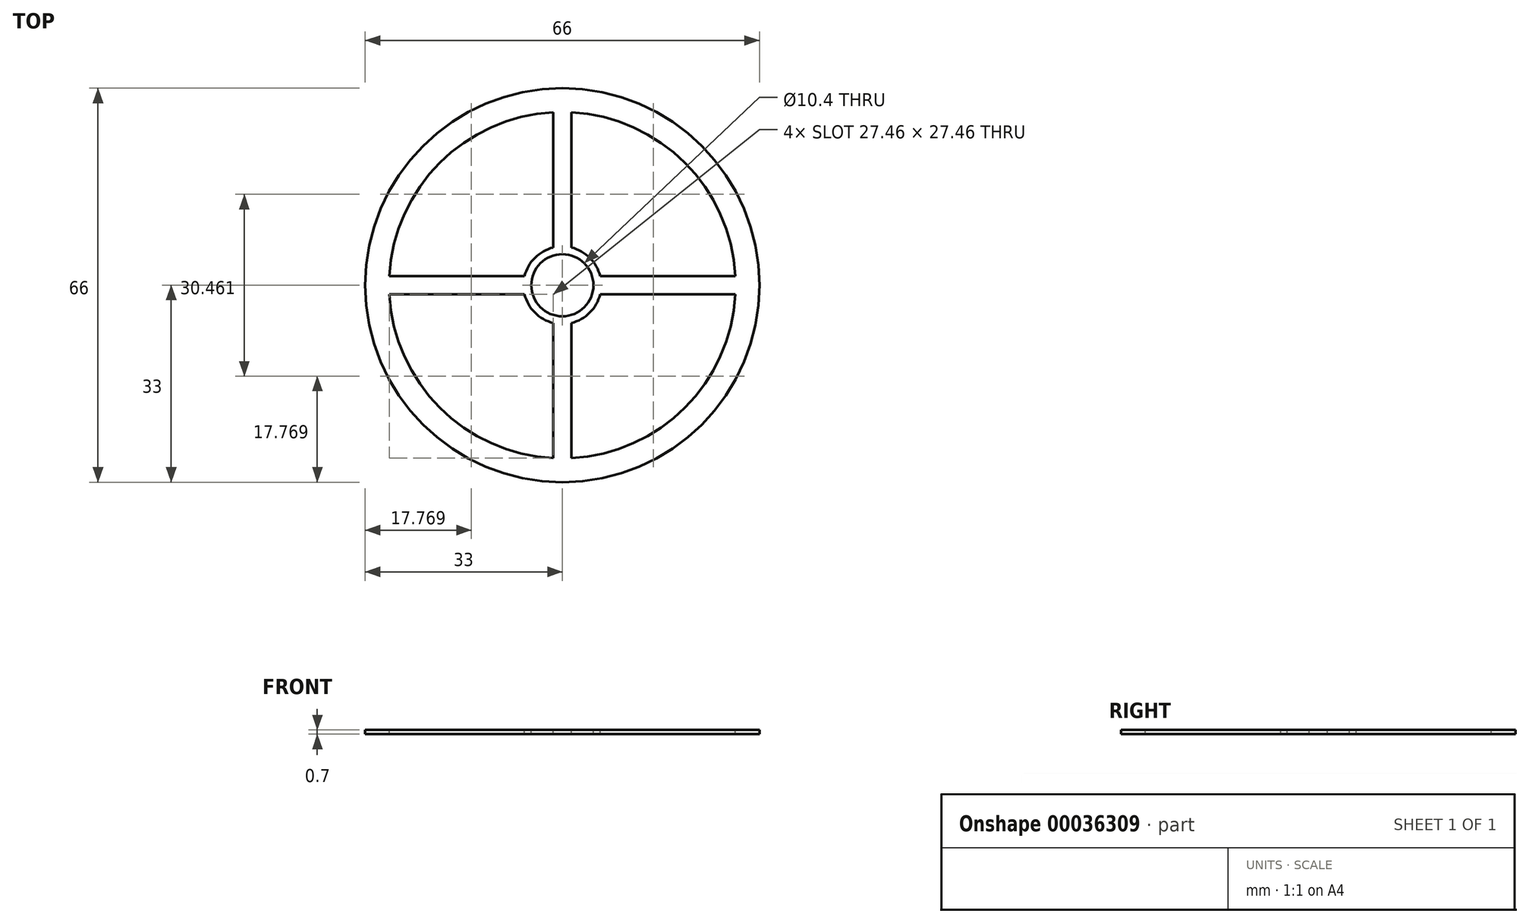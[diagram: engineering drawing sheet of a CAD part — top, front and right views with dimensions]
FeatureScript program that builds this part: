
annotation { "Feature Type Name" : "Feature", "Feature Type Description" : "" }
export const myFeature = defineFeature(function(context is Context, id is Id, definition is map)
    precondition{}
    {
        {
            var Q0;
            Q0=qCreatedBy(makeId("Top.planeOp"),FACE);
            var sketch = newSketch(context, id + "F0", { "sketchPlane" : qUnion([Q0])});
            skCircle(sketch, "E0", {"center": v(0, 0) * mm, "radius": 33 * mm});
            skSolve(sketch);
        }
        {
            var Q0;
            Q0=qSketchRegion(id+"F0",true);
            extrude(context, id + "F1", {"entities" : qUnion([Q0]), "depth" : 0.7 * mm});
        }
        {
            var Q0;
            Q0=makeQuery(id+"F1.opExtrude","CAP_FACE",FACE,{"disambiguationData":[OSD([sQuery(id+"F0.wireOp",EDGE,"E0")])],"isStart":false});
            var sketch = newSketch(context, id + "F2", { "sketchPlane" : qUnion([Q0])});
            skCircle(sketch, "E1", {"center": v(0, 0) * mm, "radius": 5.2 * mm});
            skSolve(sketch);
        }
        {
            var Q0;
            Q0=makeQuery(id+"F2.imprint","IMPRINT",FACE,{"disambiguationData":[TD([[makeQuery(id+"F2.imprint","IMPRINT",EDGE,{"derivedFrom":sQuery(id+"F2.wireOp",EDGE,"E1")}),1.0]])]});
            extrude(context, id + "F3", {"entities" : qUnion([Q0]), "operationType" : NewBodyOperationType.REMOVE, "endBound" : BoundingType.UP_TO_NEXT, "oppositeDirection" : true, "depth" : 25 * mm});
        }
        {
            var Q0;
            Q0=makeQuery(id+"F1.opExtrude","CAP_FACE",FACE,{"disambiguationData":[OSD([sQuery(id+"F0.wireOp",EDGE,"E0")])],"isStart":false});
            var sketch = newSketch(context, id + "F4", { "sketchPlane" : qUnion([Q0])});
            skCircle(sketch, "E2", {"center": v(0, 0) * mm, "radius": 29 * mm});
            skCircle(sketch, "E3", {"center": v(0, 0) * mm, "radius": 6.5 * mm});
            skLineSegment(sketch, "E4", {"start": v(0, -6.5) * mm, "end": v(0, -29) * mm, "construction": true});
            skLineSegment(sketch, "E5", {"start": v(-6.5, 0) * mm, "end": v(-29, 0) * mm, "construction": true});
            skLineSegment(sketch, "E6", {"start": v(0, 6.5) * mm, "end": v(0, 29) * mm, "construction": true});
            skLineSegment(sketch, "E7", {"start": v(6.5, 0) * mm, "end": v(29, 0) * mm, "construction": true});
            skLineSegment(sketch, "E8.0", {"start": v(1.5, 6.32) * mm, "end": v(1.5, 28.96) * mm});
            skLineSegment(sketch, "E9.0", {"start": v(-1.5, 6.32) * mm, "end": v(-1.5, 28.96) * mm});
            skLineSegment(sketch, "E10", {"start": v(1.5, -6.32) * mm, "end": v(1.5, -28.96) * mm});
            skLineSegment(sketch, "E11", {"start": v(-1.5, -6.32) * mm, "end": v(-1.5, -28.96) * mm});
            skLineSegment(sketch, "E12.0", {"start": v(6.32, 1.5) * mm, "end": v(28.96, 1.5) * mm});
            skLineSegment(sketch, "E13.0", {"start": v(6.32, -1.5) * mm, "end": v(28.96, -1.5) * mm});
            skLineSegment(sketch, "E14", {"start": v(-6.32, 1.5) * mm, "end": v(-28.96, 1.5) * mm});
            skLineSegment(sketch, "E15", {"start": v(-6.32, -1.5) * mm, "end": v(-28.96, -1.5) * mm});
            skSolve(sketch);
        }
        {
            var Q0;
            {var subQ1=sQuery(id+"F4.wireOp",EDGE,"E9.0");Q0=makeQuery(id+"F4.imprint","IMPRINT",FACE,{"disambiguationData":[TD([[makeQuery(id+"F4.imprint","IMPRINT",EDGE,{"derivedFrom":subQ1}),1.0]])]});}
            var Q1;
            {var subQ1=sQuery(id+"F4.wireOp",EDGE,"E8.0");Q1=makeQuery(id+"F4.imprint","IMPRINT",FACE,{"disambiguationData":[TD([[makeQuery(id+"F4.imprint","IMPRINT",EDGE,{"derivedFrom":subQ1}),-1.0]])]});}
            var Q2;
            {var subQ1=sQuery(id+"F4.wireOp",EDGE,"E10");Q2=makeQuery(id+"F4.imprint","IMPRINT",FACE,{"disambiguationData":[TD([[makeQuery(id+"F4.imprint","IMPRINT",EDGE,{"derivedFrom":subQ1}),1.0]])]});}
            var Q3;
            {var subQ1=sQuery(id+"F4.wireOp",EDGE,"E11");Q3=makeQuery(id+"F4.imprint","IMPRINT",FACE,{"disambiguationData":[TD([[makeQuery(id+"F4.imprint","IMPRINT",EDGE,{"derivedFrom":subQ1}),-1.0]])]});}
            extrude(context, id + "F5", {"entities" : qUnion([Q0, Q1, Q2, Q3]), "operationType" : NewBodyOperationType.REMOVE, "endBound" : BoundingType.UP_TO_NEXT, "oppositeDirection" : true, "depth" : 25 * mm});
        }
    });
